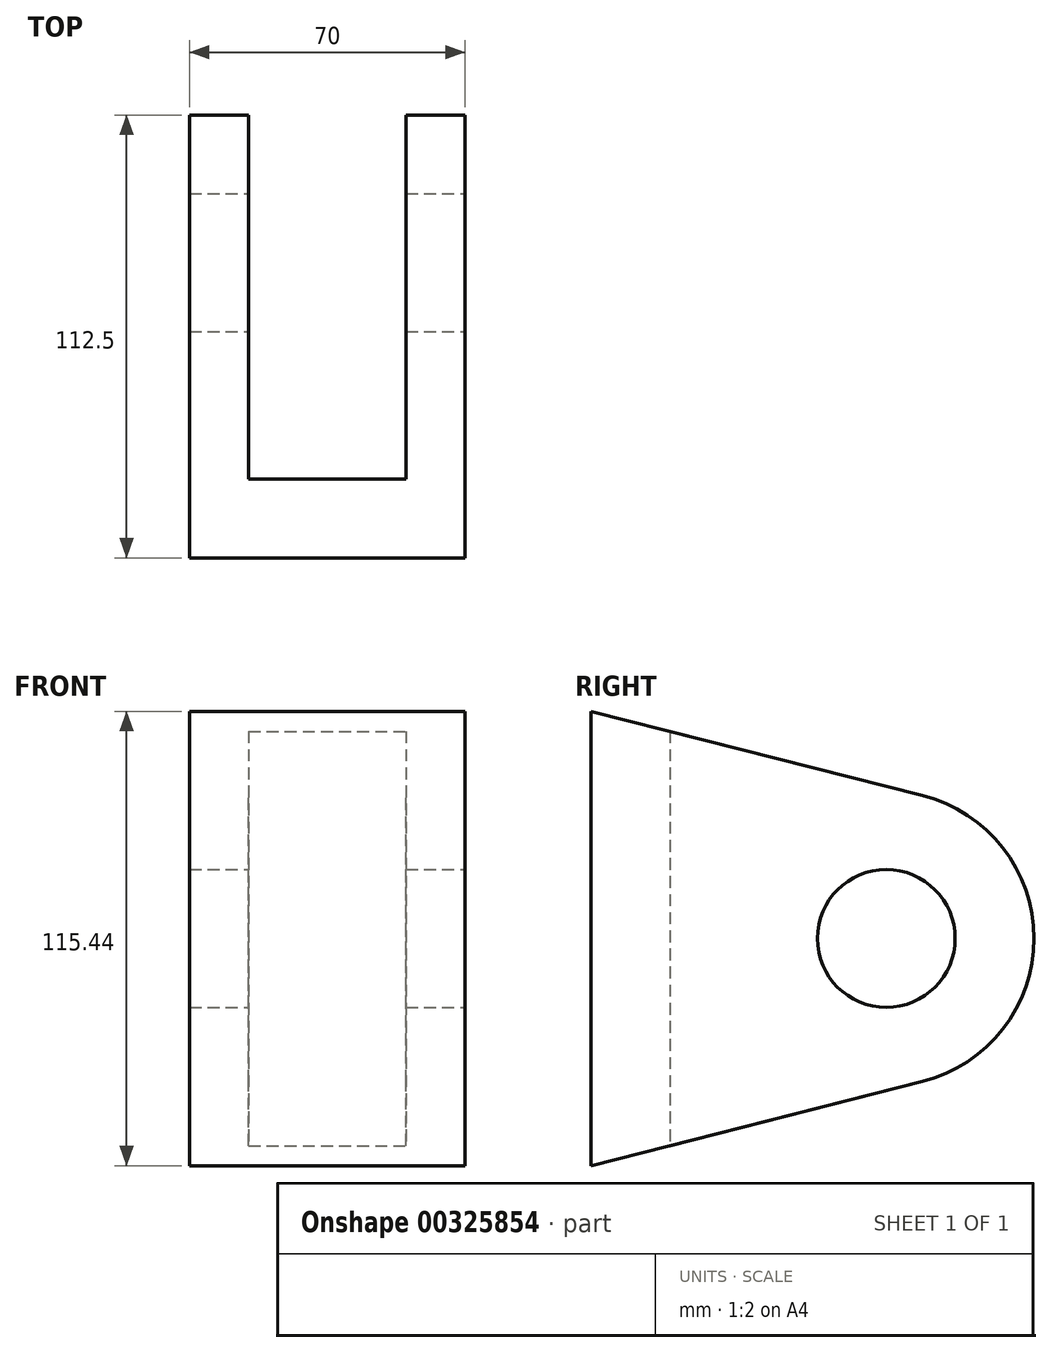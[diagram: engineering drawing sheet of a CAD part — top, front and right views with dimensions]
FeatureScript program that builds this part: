
annotation { "Feature Type Name" : "Feature", "Feature Type Description" : "" }
export const myFeature = defineFeature(function(context is Context, id is Id, definition is map)
    precondition{}
    {
        {
            var Q0;
            Q0=qCreatedBy(makeId("Right.planeOp"),FACE);
            var sketch = newSketch(context, id + "F0", { "sketchPlane" : qUnion([Q0])});
            skLineSegment(sketch, "E0.left", {"start": v(0, 0) * mm, "end": v(0, 75.44) * mm});
            skArc(sketch, "E1", {"start": v(84.22, 1.37) * mm, "mid": v(112.5, 37.72) * mm, "end": v(84.22, 74.07) * mm});
            skLineSegment(sketch, "E2", {"start": v(0, 75.44) * mm, "end": v(0, 95.44) * mm});
            skLineSegment(sketch, "E3", {"start": v(0, 95.44) * mm, "end": v(0, 0) * mm});
            skLineSegment(sketch, "E4", {"start": v(0, 0) * mm, "end": v(0, -20) * mm});
            skLineSegment(sketch, "E5", {"start": v(0, -20) * mm, "end": v(84.22, 1.37) * mm});
            skLineSegment(sketch, "E6", {"start": v(0, 95.44) * mm, "end": v(84.22, 74.07) * mm});
            skLineSegment(sketch, "E7", {"start": v(0, 37.72) * mm, "end": v(75, 37.72) * mm});
            skPoint(sketch, "E7.endSnap0", {"position": v(0, 37.72) * mm});
            skSolve(sketch);
        }
        {
            var Q0;
            Q0=makeQuery(id+"F0.imprint","IMPRINT",FACE,{"disambiguationData":[TD([[makeQuery(id+"F0.imprint","IMPRINT",EDGE,{"derivedFrom":sQuery(id+"F0.wireOp",EDGE,"E1")}),1.0]])]});
            extrude(context, id + "F1", {"entities" : qUnion([Q0]), "endBound" : BoundingType.SYMMETRIC, "depth" : 70 * mm});
        }
        {
            var Q0;
            Q0=qCreatedBy(makeId("Right.planeOp"),FACE);
            var sketch = newSketch(context, id + "F2", { "sketchPlane" : qUnion([Q0])});
            skLineSegment(sketch, "E8.bottom", {"start": v(20, 128.18) * mm, "end": v(183.4, 128.18) * mm});
            skLineSegment(sketch, "E8.top", {"start": v(20, -44.9) * mm, "end": v(183.4, -44.9) * mm});
            skLineSegment(sketch, "E8.left", {"start": v(20, 128.18) * mm, "end": v(20, -44.9) * mm});
            skLineSegment(sketch, "E8.right", {"start": v(183.4, 128.18) * mm, "end": v(183.4, -44.9) * mm});
            skSolve(sketch);
        }
        {
            var Q0;
            Q0=makeQuery(id+"F2.imprint","IMPRINT",FACE,{"disambiguationData":[TD([[makeQuery(id+"F2.imprint","IMPRINT",EDGE,{"derivedFrom":sQuery(id+"F2.wireOp",EDGE,"E8.bottom")}),-1.0]])]});
            extrude(context, id + "F3", {"entities" : qUnion([Q0]), "operationType" : NewBodyOperationType.REMOVE, "endBound" : BoundingType.SYMMETRIC, "oppositeDirection" : true, "depth" : 40 * mm});
        }
        {
            var Q0;
            Q0=makeQuery(id+"F1.opExtrude","CAP_FACE",FACE,{"disambiguationData":[OSD([sQuery(id+"F0.wireOp",EDGE,"E1"),sQuery(id+"F0.wireOp",EDGE,"E3"),sQuery(id+"F0.wireOp",EDGE,"E4"),sQuery(id+"F0.wireOp",EDGE,"E5"),sQuery(id+"F0.wireOp",EDGE,"E6")])],"isStart":false});
            var sketch = newSketch(context, id + "F4", { "sketchPlane" : qUnion([Q0])});
            skCircle(sketch, "E9", {"center": v(75, 37.72) * mm, "radius": 17.5 * mm});
            skSolve(sketch);
        }
        {
            var Q0;
            Q0=makeQuery(id+"F4.imprint","IMPRINT",FACE,{"disambiguationData":[TD([[makeQuery(id+"F4.imprint","IMPRINT",EDGE,{"derivedFrom":sQuery(id+"F4.wireOp",EDGE,"E9")}),1.0]])]});
            extrude(context, id + "F5", {"entities" : qUnion([Q0]), "operationType" : NewBodyOperationType.REMOVE, "oppositeDirection" : true, "depth" : 100 * mm});
        }
    });
